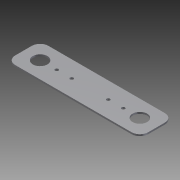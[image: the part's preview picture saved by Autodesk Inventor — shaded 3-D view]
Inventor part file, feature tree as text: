
AUTODESK INVENTOR PART (.ipt)
format: ipt  version: 2012 (Build 160160000, 160)  size: 103,424 bytes
history: native  units: mm
features: extrude x1, sketch x1
ambient origin geometry x8: Origin, YZ Plane, XZ Plane, XY Plane, X Axis, Y Axis, Z Axis, Center Point
bodies: Solid1 (feature_tree)
feature tree (2):
  extrude  "Extrusion1"  Depth=1.0mm TaperAngle=0.0deg
  sketch  "Sketch1"  dims[d109=10.0mm d110=10.0mm d111=8.77mm d112=8.77mm d113=2.0mm d114=2.0mm d115=10.0mm d116=9.0mm d117=2.0mm d118=2.0mm d119=10.0mm d120=9.0mm d121=60.0mm d126=10.0mm d399=1.0mm d400=0.0mm]
